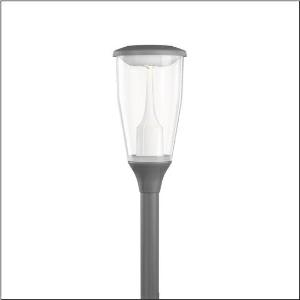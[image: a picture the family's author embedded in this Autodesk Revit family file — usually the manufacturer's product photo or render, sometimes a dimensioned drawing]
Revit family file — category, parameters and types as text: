
# Revit family: dl_11_iq___st1_2a_5xa5575kf14h000022_bb26
name_source: partatom
category: Lighting Fixtures
units: mm (PartAtom-declared; Revit-internal decimal feet)

## family parameters
Cut with Voids When Loaded = No
Host = Face
Light Source = No
Part Type = Normal
Room Calculation Point = No
Round Connector Dimension = Use Diameter
Shared = No

## types (1)
- --- (1 x LED, 1560 lm, 10 W, 4000K)
    Apparent Load = 10 VA
    CIE Flux Codes = 24 63 94 96 100
    Color Rendering = 70
    Color Temperature = 4000K
    Default Elevation = 1800 mm
    Description = DL 11 iQ, mast luminaire, Module 540 iQ-SR, primary light control with 3 zone facetted reflector, of plastic, silver coated, highly specular, structured, primary optical cover: cover, of PMMA, transparent, light distribution: ST1.2a, light emission: direct distribution, primary light characteristic: asymmetric, installation type: post-top, LED, High Power LED, light colour: 740, colour temperature: 4000K, control: Street-Remote, Auto-Match, Temp-Guard, Lumen-Switch, Night-Set, Smart-Wire, Light-Fading, Desk-Remote (wireless, voltage-free reading and setting of iQ features in the workshop via application-optimized NFC function/RFID function), optimised constant luminous flux control (CLO 2.0), mains connection: 220..240V, AC, 50/60Hz, connection cable pre-assembled, cable length: 5,5m, start of lifetime: 10W, end of service life: 10W, luminaire housing, upper part, of diecast aluminium, coated, Siteco® metallic grey (DB 702S), spigot size: 76mm (post-top), post-top mast mounting element, of diecast aluminium, coated, Siteco® metallic grey (DB 702S), Module 540 iQ-SR, traffic white (RAL 9016), equipment: standard, protection rating (complete): IP66, insulation class (complete): insulation class II (safety insulation), certification: CE, ENEC, ENEC+, VDE, packaging unit: 1 piece

Light Distribution: ST1.2a
    Height = 665 mm
    Lamp = 1 x LED
    Lamp Light Flux = 1560 lm
    Lamp Power = 10 W
    Lamp count = 1
    Length = 334 mm
    Luminous efficacy = 156 lm/W
    Manufacturer = Siteco
    ModVariant = No
    Model = 5XA5575KF14H000022
    Number of Poles = 1
    OnlyDefault = Yes
    Power Factor = 1
    Product Name = DL 11 iQ | ST1.2a
    Product group = mast luminaire | pylon top
    ProductGroupID = 6100
    Protection Class = Protection class II
    Protection Degree = IP 66
    RLX_Detail_Level = 1
    RLX_Emergency_Light_Flux = 0 lm
    RLX_Emergency_Type = 0
    RLX_Emergency_Type_DB = No
    RlxData = <blob elided: 155817 chars, md5=1f703f1d>
    Socket = socket
    Standby Power = 0 W
    System Light Flux = 1560 lm
    System Power = 10 W
    Type Comments = factory setting: luminous flux: 100 % | dim-lin: 254 | 401 mA
    Type Image = l_1258354.jpg
    URL = http://relux.com
    VarID = @adj_025741
    Voltage = 0 V
    Weight = 0.00 kg
    Width = 0 mm  [stored 0 ft]

note: [stored X ft] marks values corroborated as IEEE doubles in the binary element streams (Revit-internal decimal feet)

## geometry (parser evidence)
native form markers: Blend x4, Sweep x11
no freeform markers — native parametric forms only
